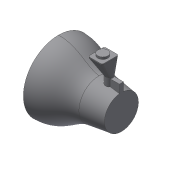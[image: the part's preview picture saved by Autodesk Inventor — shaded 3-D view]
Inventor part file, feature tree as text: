
AUTODESK INVENTOR PART (.ipt)
format: ipt  version: 2018 (Build 220112000, 112)  size: 259,072 bytes
history: native  units: mm
features: sketch x3, extrude x2, revolve x1, plane x1, imported_body x1, boolean_combine x1, projected_geometry x1
ambient origin geometry x8: Origin, YZ Plane, XZ Plane, XY Plane, X Axis, Y Axis, Z Axis, Center Point
bodies: Solid1 (feature_tree), Solid3 (feature_tree)
feature tree (10):
  revolve  "Revolution1"  [1 undecoded]
  plane  "Work Plane1"
  extrude  "Extrusion1"  Depth=45.0mm
  extrude  "Extrusion4"  Depth=70.0mm
  imported_body  "Base1"
  boolean_combine  "Combine1"
  sketch  "Sketch1"  dims[d0=125.0mm d1=40.0mm]
  sketch  "Sketch2"  dims[d2=45.0mm d3=45.0mm]
  sketch  "Sketch6"  dims[d4=10.0mm d5=70.0mm d6=22.0mm d7=70.0mm d8=90.0deg d9=17.104227mm d14=50.0mm d15=15.0mm d16=38.0mm d17=10.0mm d18=0.0mm d39=20.0mm d40=10.0mm d41=0.0mm]
  projected_geometry  "Projected Loop3"
note: 1 required parameter value undecoded (feature->parameter linkage not recoverable at this tier; creation-order binding heuristic only, values carry confidence <= 0.55)
